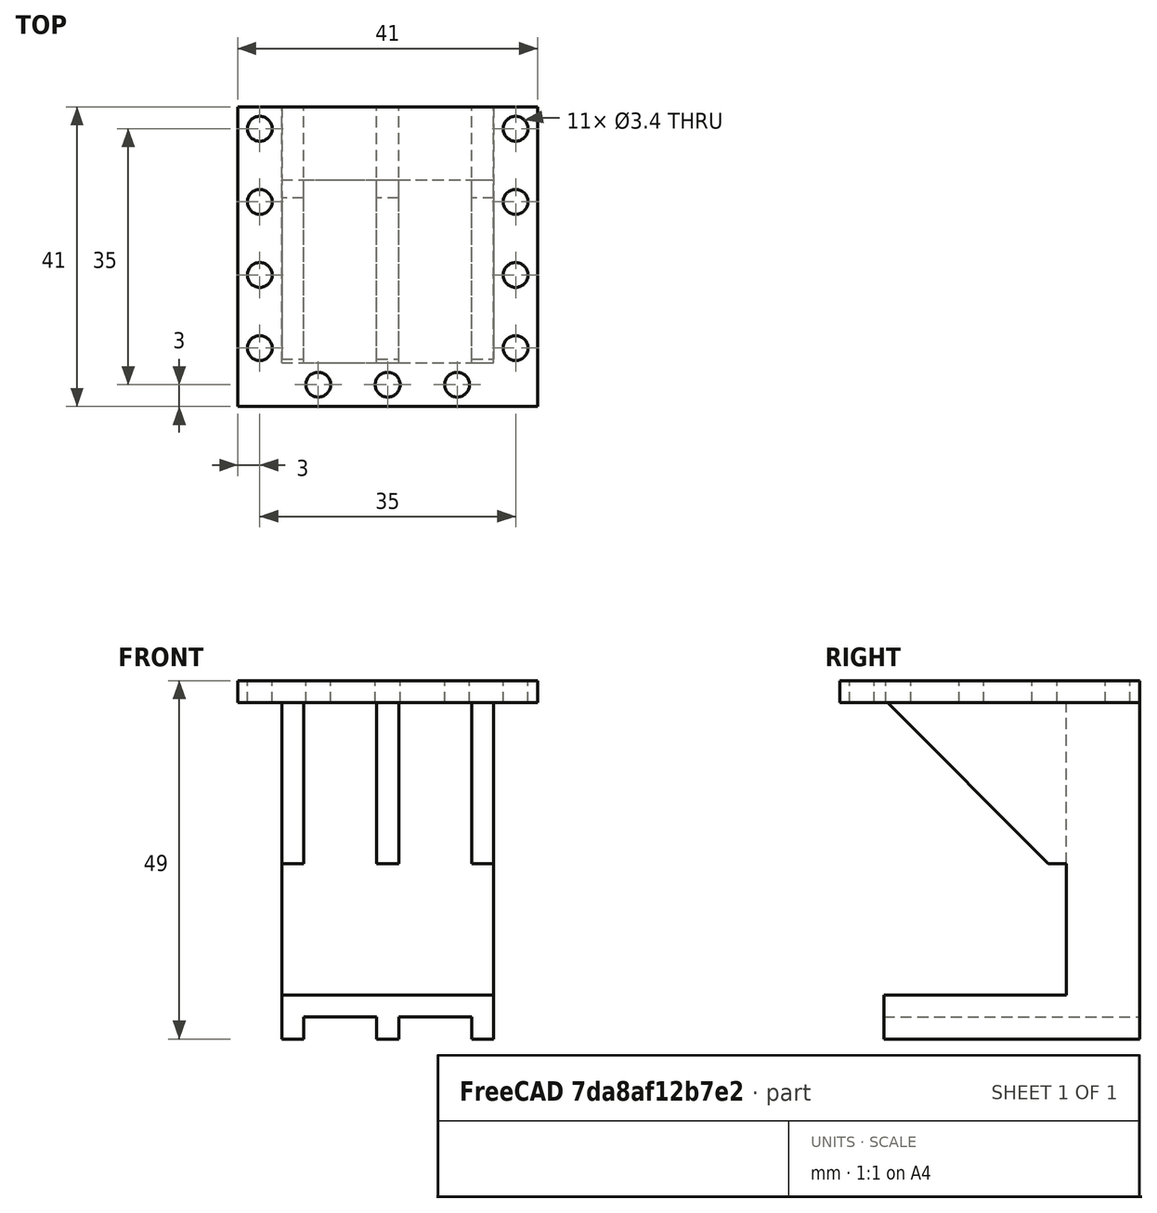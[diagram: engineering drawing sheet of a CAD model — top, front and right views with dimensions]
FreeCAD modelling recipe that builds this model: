
FCSTD DOCUMENT  (FreeCAD 0.16R6707 (Git))
Label: xmaxx-front-bracket1
License: All rights reserved
LicenseURL: http://en.wikipedia.org/wiki/All_rights_reserved
objects: Part::Cut×17, Part::Cylinder×11, Part::Box×8, Part::Fuse×1
note: 37 computed .brp shape members not serialized (recipe doc carries the construction recipe); baked Part::Feature solids carry a one-line shape summary decoded from their .brp

FEATURE [Part::Box] Box  label="Cube"
  Height = 49
  Length = 29
  Width = 35
FEATURE [Part::Box] Box001  label="Cube001"
  Height = 18
  Length = 29
  Placement = pos=(0,0,6) rot=(0,0,1;0rad)
  Width = 25
FEATURE [Part::Box] Box002  label="Cube002"
  Height = 3
  Length = 10
  Placement = pos=(3,0,0) rot=(0,0,1;0rad)
  Width = 40
FEATURE [Part::Box] Box003  label="Cube003"
  Height = 3
  Length = 10
  Placement = pos=(16,0,0) rot=(0,0,1;0rad)
  Width = 40
FEATURE [Part::Cut] Cut
  Base = -> Box
  Tool = -> Box002
FEATURE [Part::Cut] Cut001
  Base = -> Cut
  Tool = -> Box003
FEATURE [Part::Cut] Cut002
  Base = -> Cut001
  Tool = -> Box001
FEATURE [Part::Box] Box004  label="Cube004"
  Height = 34
  Length = 29
  Placement = pos=(0,7,7) rot=(1,0,0;0.785398rad)
  Width = 23
FEATURE [Part::Cut] Cut003
  Base = -> Cut002
  Tool = -> Box004
FEATURE [Part::Box] Box005  label="Cube005"
  Height = 22
  Length = 10
  Placement = pos=(3,0,24) rot=(0,0,1;0rad)
  Width = 25
FEATURE [Part::Box] Box006  label="Cube006"
  Height = 22
  Length = 10
  Placement = pos=(16,0,24) rot=(0,0,1;0rad)
  Width = 25
FEATURE [Part::Cut] Cut004
  Base = -> Cut003
  Tool = -> Box005
FEATURE [Part::Cut] Cut005
  Base = -> Cut004
  Tool = -> Box006
FEATURE [Part::Box] Box007  label="Cube007"
  Height = 3
  Length = 41
  Placement = pos=(-6,-6,46) rot=(0,0,1;0rad)
  Width = 41
FEATURE [Part::Cylinder] Cylinder
  Angle = 360
  Height = 10
  Placement = pos=(14.5,-3,41) rot=(0,0,1;0rad)
  Radius = 1.7
FEATURE [Part::Cylinder] Cylinder001
  Angle = 360
  Height = 10
  Placement = pos=(5,-3,41) rot=(0,0,1;0rad)
  Radius = 1.7
FEATURE [Part::Cylinder] Cylinder002
  Angle = 360
  Height = 10
  Placement = pos=(24,-3,41) rot=(0,0,1;0rad)
  Radius = 1.7
FEATURE [Part::Cylinder] Cylinder003
  Angle = 360
  Height = 10
  Placement = pos=(-3,32,41) rot=(0,0,1;0rad)
  Radius = 1.7
FEATURE [Part::Cylinder] Cylinder004
  Angle = 360
  Height = 10
  Placement = pos=(-3,22,41) rot=(0,0,1;0rad)
  Radius = 1.7
FEATURE [Part::Cylinder] Cylinder005
  Angle = 360
  Height = 10
  Placement = pos=(-3,12,41) rot=(0,0,1;0rad)
  Radius = 1.7
FEATURE [Part::Cylinder] Cylinder006
  Angle = 360
  Height = 10
  Placement = pos=(-3,2,41) rot=(0,0,1;0rad)
  Radius = 1.7
FEATURE [Part::Cylinder] Cylinder007
  Angle = 360
  Height = 10
  Placement = pos=(32,32,41) rot=(0,0,1;0rad)
  Radius = 1.7
FEATURE [Part::Cylinder] Cylinder008
  Angle = 360
  Height = 10
  Placement = pos=(32,22,41) rot=(0,0,1;0rad)
  Radius = 1.7
FEATURE [Part::Cylinder] Cylinder009
  Angle = 360
  Height = 10
  Placement = pos=(32,12,41) rot=(0,0,1;0rad)
  Radius = 1.7
FEATURE [Part::Cylinder] Cylinder010
  Angle = 360
  Height = 10
  Placement = pos=(32,2,41) rot=(0,0,1;0rad)
  Radius = 1.7
FEATURE [Part::Cut] Cut006
  Base = -> Box007
  Tool = -> Cylinder
FEATURE [Part::Cut] Cut007
  Base = -> Cut006
  Tool = -> Cylinder001
FEATURE [Part::Cut] Cut008
  Base = -> Cut007
  Tool = -> Cylinder002
FEATURE [Part::Cut] Cut009
  Base = -> Cut008
  Tool = -> Cylinder003
FEATURE [Part::Cut] Cut010
  Base = -> Cut009
  Tool = -> Cylinder004
FEATURE [Part::Cut] Cut011
  Base = -> Cut010
  Tool = -> Cylinder005
FEATURE [Part::Cut] Cut012
  Base = -> Cut011
  Tool = -> Cylinder006
FEATURE [Part::Cut] Cut013
  Base = -> Cut012
  Tool = -> Cylinder007
FEATURE [Part::Cut] Cut014
  Base = -> Cut013
  Tool = -> Cylinder008
FEATURE [Part::Cut] Cut015
  Base = -> Cut014
  Tool = -> Cylinder009
FEATURE [Part::Cut] Cut016
  Base = -> Cut015
  Tool = -> Cylinder010
FEATURE [Part::Fuse] Fusion
  Base = -> Cut005
  Tool = -> Cut016
